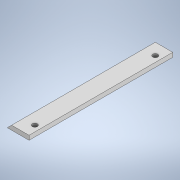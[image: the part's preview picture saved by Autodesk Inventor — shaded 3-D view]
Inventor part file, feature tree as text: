
AUTODESK INVENTOR PART (.ipt)
format: ipt  version: 2020 (Build 240168000, 168)  size: 112,640 bytes
history: native  units: mm
features: extrude x2, sketch x2
ambient origin geometry x8: Origin, YZ Plane, XZ Plane, XY Plane, X Axis, Y Axis, Z Axis, Center Point
bodies: Solid1 (feature_tree)
feature tree (4):
  extrude  "Extrusion1"  Depth=15.0mm
  extrude  "Extrusion2"  Depth=3.0mm
  sketch  "Sketch1"  dims[d0=99.0mm d1=15.0mm]
  sketch  "Sketch2"  dims[d2=8.0mm d3=83.0mm d4=4.0mm d5=4.0mm d6=3.5mm d7=3.5mm d8=3.0mm d9=0.0mm d10=45.0deg d11=3.0mm d12=0.0mm]
